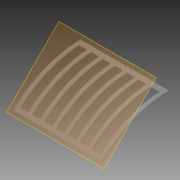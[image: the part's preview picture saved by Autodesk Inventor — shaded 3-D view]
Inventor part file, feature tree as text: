
AUTODESK INVENTOR PART (.ipt)
format: ipt  version: 2013 (Build 170138000, 138)  size: 147,968 bytes
history: native  units: in
note: dims shown in document units (in); Inventor stores cm internally (conversion verified against a paired STEP export)
features: extrude x2, plane x2, sketch x2
ambient origin geometry x8: Origin, YZ Plane, XZ Plane, XY Plane, X Axis, Y Axis, Z Axis, Center Point
bodies: Solid1 (feature_tree)
feature tree (6):
  extrude  "Extrusion1"  Depth=0.0625in
  plane  "Work Plane2"
  extrude  "Extrusion2"  Depth=11.125in TaperAngle=0.0deg
  sketch  "Sketch1"  dims[d0=23.75in d1=0.0625in]
  plane  "Work Plane1"
  sketch  "Sketch2"  dims[d2=45.0deg d3=11.125in d4=0.0in d5=90.0deg d6=8.441in d7=11.125in d8=0.5in d9=1.0in d10=0.5in d11=1.0in d12=0.5in d13=1.0in d14=0.5in d15=1.0in d16=0.5in d17=1.0in d18=0.5in d19=1.0in d20=0.5in d21=190000.0in d22=0.0in]
